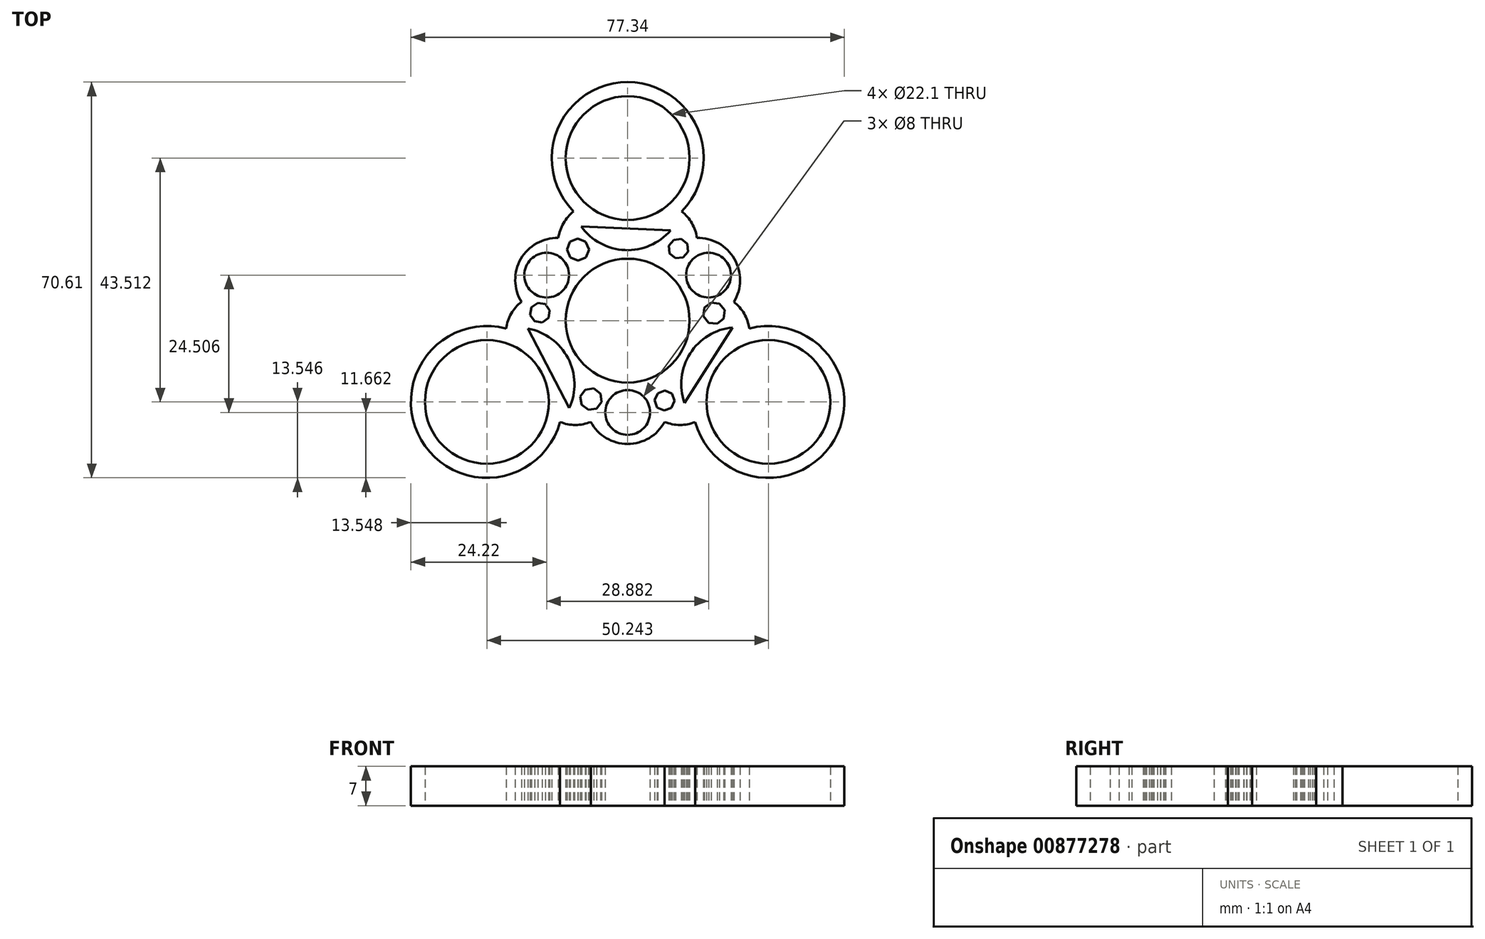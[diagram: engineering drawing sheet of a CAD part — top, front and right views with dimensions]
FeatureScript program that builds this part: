
annotation { "Feature Type Name" : "Feature", "Feature Type Description" : "" }
export const myFeature = defineFeature(function(context is Context, id is Id, definition is map)
    precondition{}
    {
        {
            var Q0;
            Q0=qCreatedBy(makeId("Top.planeOp"),FACE);
            var sketch = newSketch(context, id + "F0", { "sketchPlane" : qUnion([Q0])});
            skCircle(sketch, "E0", {"center": v(0, 0) * mm, "radius": 11.05 * mm});
            skCircle(sketch, "E1", {"center": v(0, 29) * mm, "radius": 11.05 * mm});
            skArc(sketch, "E2.1.1", {"start": v(-21.7, -1.4) * mm, "mid": v(-36.86, -21.28) * mm, "end": v(-12.06, -18.1) * mm});
            skCircle(sketch, "E2.2.0", {"center": v(25.12, -14.5) * mm, "radius": 11.05 * mm});
            skArc(sketch, "E2.2.1", {"start": v(12.06, -18.1) * mm, "mid": v(36.86, -21.28) * mm, "end": v(21.7, -1.4) * mm});
            skArc(sketch, "E3.1.3.0", {"start": v(-12.38, 14.75) * mm, "mid": v(-19.06, 11) * mm, "end": v(-18.96, 3.34) * mm});
            skArc(sketch, "E3.1.4.0", {"start": v(-18.96, 3.34) * mm, "mid": v(-20.78, 1.23) * mm, "end": v(-21.7, -1.4) * mm});
            skArc(sketch, "E3.1.5.0", {"start": v(-12.06, -18.1) * mm, "mid": v(-9.32, -18.61) * mm, "end": v(-6.59, -18.1) * mm});
            skArc(sketch, "E3.1.6.0", {"start": v(-6.59, -18.1) * mm, "mid": v(0, -22) * mm, "end": v(6.59, -18.1) * mm});
            skArc(sketch, "E3.1.7.0", {"start": v(6.59, -18.1) * mm, "mid": v(9.32, -18.61) * mm, "end": v(12.06, -18.1) * mm});
            skArc(sketch, "E4.trimOffspring", {"start": v(-9.64, 19.49) * mm, "mid": v(-11.46, 17.38) * mm, "end": v(-12.38, 14.75) * mm});
            skArc(sketch, "E5.trimOffspring", {"start": v(12.38, 14.75) * mm, "mid": v(11.46, 17.38) * mm, "end": v(9.64, 19.49) * mm});
            skArc(sketch, "E6.trimOffspring", {"start": v(-13.55, -0.18) * mm, "mid": v(-12.3, -0.24) * mm, "end": v(-11.05, -0.1) * mm});
            skArc(sketch, "E7.trimOffspring", {"start": v(18.96, 3.34) * mm, "mid": v(19.06, 11) * mm, "end": v(12.38, 14.75) * mm});
            skArc(sketch, "E8.trimOffspring", {"start": v(21.7, -1.4) * mm, "mid": v(20.78, 1.23) * mm, "end": v(18.96, 3.34) * mm});
            skCircle(sketch, "E9", {"center": v(14.43, 8.12) * mm, "radius": 4 * mm});
            skCircle(sketch, "E10", {"center": v(0, -16.39) * mm, "radius": 4 * mm});
            skPoint(sketch, "E10.centerSnap0", {"position": v(0, -22) * mm});
            skCircle(sketch, "E11", {"center": v(-14.45, 8.12) * mm, "radius": 4 * mm});
            skCircle(sketch, "E12", {"center": v(-25.12, -14.5) * mm, "radius": 11.05 * mm});
            skArc(sketch, "E13", {"start": v(9.64, 19.49) * mm, "mid": v(0, 42.56) * mm, "end": v(-9.64, 19.49) * mm});
            skArc(sketch, "E14", {"start": v(18.7, -1.22) * mm, "mid": v(11.14, -5.87) * mm, "end": v(10.12, -14.7) * mm});
            skLineSegment(sketch, "E15", {"start": v(10.12, -14.7) * mm, "end": v(18.7, -1.22) * mm});
            skArc(sketch, "E16.1.0", {"start": v(-8.3, 16.8) * mm, "mid": v(-0.48, 12.58) * mm, "end": v(7.66, 16.1) * mm});
            skLineSegment(sketch, "E16.1.1", {"start": v(7.66, 16.1) * mm, "end": v(-8.3, 16.8) * mm});
            skArc(sketch, "E16.2.0", {"start": v(-10.4, -15.58) * mm, "mid": v(-10.66, -6.7) * mm, "end": v(-17.78, -1.42) * mm});
            skLineSegment(sketch, "E16.2.1", {"start": v(-17.78, -1.42) * mm, "end": v(-10.4, -15.58) * mm});
            skCircle(sketch, "E17.cCircle", {"center": v(-8.87, 12.68) * mm, "radius": 1.82 * mm, "construction": true});
            skLineSegment(sketch, "E17.0", {"start": v(-6.9, 12.7) * mm, "end": v(-7.46, 11.3) * mm});
            skLineSegment(sketch, "E17.1", {"start": v(-7.46, 11.3) * mm, "end": v(-8.85, 10.72) * mm});
            skLineSegment(sketch, "E17.2", {"start": v(-8.85, 10.72) * mm, "end": v(-10.24, 11.27) * mm});
            skLineSegment(sketch, "E17.3", {"start": v(-10.24, 11.27) * mm, "end": v(-10.84, 12.66) * mm});
            skLineSegment(sketch, "E17.4", {"start": v(-10.84, 12.66) * mm, "end": v(-10.28, 14.06) * mm});
            skLineSegment(sketch, "E17.5", {"start": v(-10.28, 14.06) * mm, "end": v(-8.9, 14.65) * mm});
            skLineSegment(sketch, "E17.6", {"start": v(-8.9, 14.65) * mm, "end": v(-7.5, 14.1) * mm});
            skLineSegment(sketch, "E17.7", {"start": v(-7.5, 14.1) * mm, "end": v(-6.9, 12.7) * mm});
            skPoint(sketch, "E17.0.midPoint", {"position": v(-7.18, 12) * mm});
            skCircle(sketch, "E18.1.0", {"center": v(-6.55, -14.02) * mm, "radius": 1.82 * mm, "construction": true});
            skLineSegment(sketch, "E18.1.1", {"start": v(-8.45, -13.54) * mm, "end": v(-7.55, -12.33) * mm});
            skLineSegment(sketch, "E18.1.2", {"start": v(-8.24, -15.03) * mm, "end": v(-8.45, -13.54) * mm});
            skLineSegment(sketch, "E18.1.3", {"start": v(-7.03, -15.93) * mm, "end": v(-8.24, -15.03) * mm});
            skLineSegment(sketch, "E18.1.4", {"start": v(-5.54, -15.71) * mm, "end": v(-7.03, -15.93) * mm});
            skLineSegment(sketch, "E18.1.5", {"start": v(-4.64, -14.5) * mm, "end": v(-5.54, -15.71) * mm});
            skLineSegment(sketch, "E18.1.6", {"start": v(-4.86, -13.02) * mm, "end": v(-4.64, -14.5) * mm});
            skLineSegment(sketch, "E18.1.7", {"start": v(-6.06, -12.12) * mm, "end": v(-4.86, -13.02) * mm});
            skLineSegment(sketch, "E18.1.8", {"start": v(-7.55, -12.33) * mm, "end": v(-6.06, -12.12) * mm});
            skCircle(sketch, "E18.2.0", {"center": v(15.42, 1.34) * mm, "radius": 1.82 * mm, "construction": true});
            skLineSegment(sketch, "E18.2.1", {"start": v(15.95, -0.55) * mm, "end": v(14.46, -0.38) * mm});
            skLineSegment(sketch, "E18.2.2", {"start": v(17.13, 0.38) * mm, "end": v(15.95, -0.55) * mm});
            skLineSegment(sketch, "E18.2.3", {"start": v(17.31, 1.87) * mm, "end": v(17.13, 0.38) * mm});
            skLineSegment(sketch, "E18.2.4", {"start": v(16.38, 3.06) * mm, "end": v(17.31, 1.87) * mm});
            skLineSegment(sketch, "E18.2.5", {"start": v(14.89, 3.23) * mm, "end": v(16.38, 3.06) * mm});
            skLineSegment(sketch, "E18.2.6", {"start": v(13.7, 2.3) * mm, "end": v(14.89, 3.23) * mm});
            skLineSegment(sketch, "E18.2.7", {"start": v(13.52, 0.8) * mm, "end": v(13.7, 2.3) * mm});
            skLineSegment(sketch, "E18.2.8", {"start": v(14.46, -0.38) * mm, "end": v(13.52, 0.8) * mm});
            skCircle(sketch, "E19.cCircle", {"center": v(9.06, 12.84) * mm, "radius": 1.65 * mm, "construction": true});
            skLineSegment(sketch, "E19.0", {"start": v(10.77, 12.32) * mm, "end": v(9.9, 11.26) * mm});
            skLineSegment(sketch, "E19.1", {"start": v(9.9, 11.26) * mm, "end": v(8.54, 11.12) * mm});
            skLineSegment(sketch, "E19.2", {"start": v(8.54, 11.12) * mm, "end": v(7.48, 12) * mm});
            skLineSegment(sketch, "E19.3", {"start": v(7.48, 12) * mm, "end": v(7.35, 13.36) * mm});
            skLineSegment(sketch, "E19.4", {"start": v(7.35, 13.36) * mm, "end": v(8.22, 14.42) * mm});
            skLineSegment(sketch, "E19.5", {"start": v(8.22, 14.42) * mm, "end": v(9.58, 14.55) * mm});
            skLineSegment(sketch, "E19.6", {"start": v(9.58, 14.55) * mm, "end": v(10.64, 13.68) * mm});
            skLineSegment(sketch, "E19.7", {"start": v(10.64, 13.68) * mm, "end": v(10.77, 12.32) * mm});
            skPoint(sketch, "E19.0.midPoint", {"position": v(10.34, 11.79) * mm});
            skLineSegment(sketch, "E20.1.0", {"start": v(-16.6, -0.1) * mm, "end": v(-17.4, 1.02) * mm});
            skLineSegment(sketch, "E20.1.1", {"start": v(-15.24, -0.32) * mm, "end": v(-16.6, -0.1) * mm});
            skLineSegment(sketch, "E20.1.2", {"start": v(-14.13, 0.48) * mm, "end": v(-15.24, -0.32) * mm});
            skLineSegment(sketch, "E20.1.3", {"start": v(-13.9, 1.83) * mm, "end": v(-14.13, 0.48) * mm});
            skLineSegment(sketch, "E20.1.4", {"start": v(-14.7, 2.95) * mm, "end": v(-13.9, 1.83) * mm});
            skLineSegment(sketch, "E20.1.5", {"start": v(-16.05, 3.17) * mm, "end": v(-14.7, 2.95) * mm});
            skCircle(sketch, "E20.1.6", {"center": v(-15.65, 1.43) * mm, "radius": 1.65 * mm, "construction": true});
            skLineSegment(sketch, "E20.1.7", {"start": v(-17.17, 2.38) * mm, "end": v(-16.05, 3.17) * mm});
            skLineSegment(sketch, "E20.1.8", {"start": v(-17.4, 1.02) * mm, "end": v(-17.17, 2.38) * mm});
            skLineSegment(sketch, "E20.2.0", {"start": v(8.38, -14.33) * mm, "end": v(7.81, -15.57) * mm});
            skLineSegment(sketch, "E20.2.1", {"start": v(7.9, -13.04) * mm, "end": v(8.38, -14.33) * mm});
            skLineSegment(sketch, "E20.2.2", {"start": v(6.65, -12.48) * mm, "end": v(7.9, -13.04) * mm});
            skLineSegment(sketch, "E20.2.3", {"start": v(5.36, -12.96) * mm, "end": v(6.65, -12.48) * mm});
            skLineSegment(sketch, "E20.2.4", {"start": v(4.8, -14.2) * mm, "end": v(5.36, -12.96) * mm});
            skLineSegment(sketch, "E20.2.5", {"start": v(5.28, -15.49) * mm, "end": v(4.8, -14.2) * mm});
            skCircle(sketch, "E20.2.6", {"center": v(6.59, -14.27) * mm, "radius": 1.65 * mm, "construction": true});
            skLineSegment(sketch, "E20.2.7", {"start": v(6.53, -16.06) * mm, "end": v(5.28, -15.49) * mm});
            skLineSegment(sketch, "E20.2.8", {"start": v(7.81, -15.57) * mm, "end": v(6.53, -16.06) * mm});
            skSolve(sketch);
        }
        {
            var Q0;
            Q0 = qSketchRegion(id + "F0", true);
            extrude(context, id + "F1", {"entities" : qUnion([Q0]), "depth" : 7 * mm, "offsetDistance" : 25 * mm});
        }
    });
